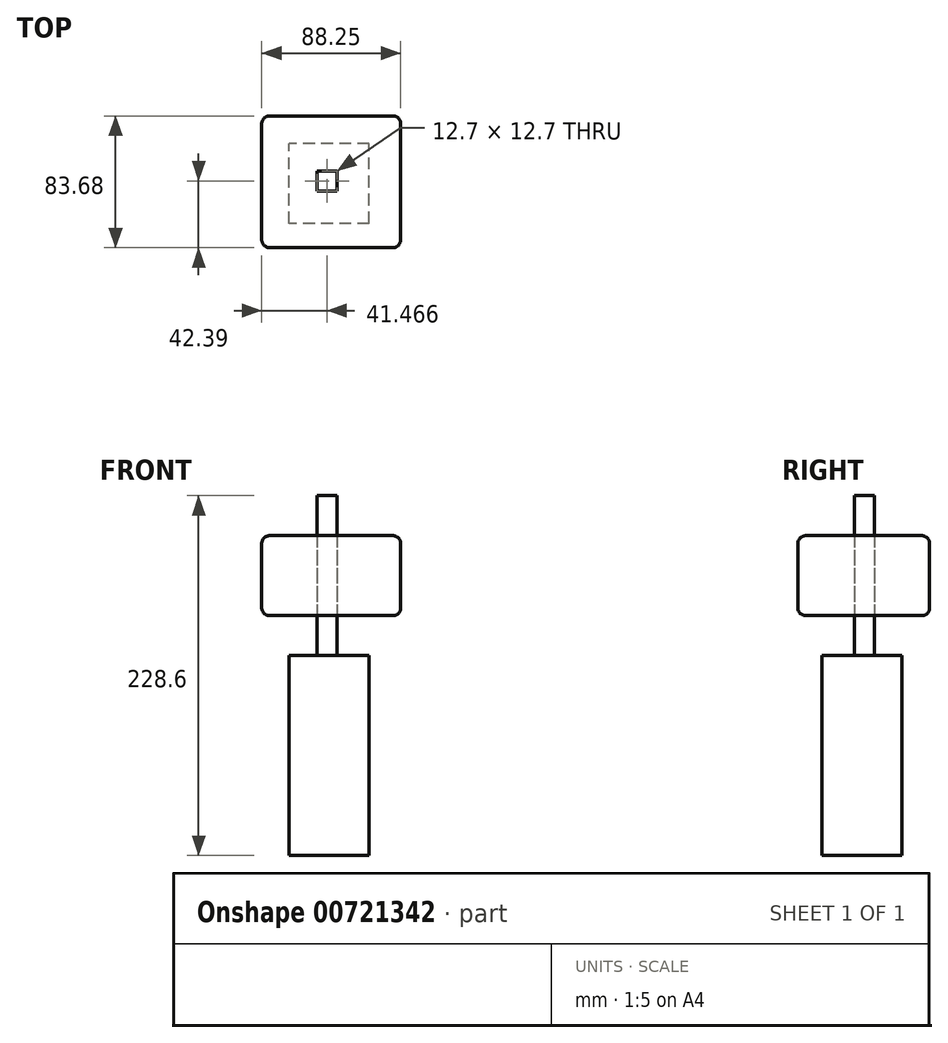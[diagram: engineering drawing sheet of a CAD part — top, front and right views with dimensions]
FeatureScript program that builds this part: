
annotation { "Feature Type Name" : "Feature", "Feature Type Description" : "" }
export const myFeature = defineFeature(function(context is Context, id is Id, definition is map)
    precondition{}
    {
        {
            var Q0;
            Q0=qCreatedBy(makeId("Front.planeOp"),FACE);
            var sketch = newSketch(context, id + "F0", { "sketchPlane" : qUnion([Q0])});
            skLineSegment(sketch, "E0.bottom", {"start": v(0, 0) * mm, "end": v(-50.8, 0) * mm});
            skLineSegment(sketch, "E0.top", {"start": v(0, 127) * mm, "end": v(-50.8, 127) * mm});
            skLineSegment(sketch, "E0.left", {"start": v(0, 0) * mm, "end": v(0, 127) * mm});
            skLineSegment(sketch, "E0.right", {"start": v(-50.8, 0) * mm, "end": v(-50.8, 127) * mm});
            skSolve(sketch);
        }
        {
            var Q0;
            Q0=makeQuery(id+"F0.imprint","IMPRINT",FACE,{"disambiguationData":[TD([[makeQuery(id+"F0.imprint","IMPRINT",EDGE,{"derivedFrom":sQuery(id+"F0.wireOp",EDGE,"E0.bottom")}),-1.0]])]});
            extrude(context, id + "F1", {"entities" : qUnion([Q0]), "depth" : 50.8 * mm, "offsetDistance" : 25.4 * mm});
        }
        {
            var Q0;
            Q0=makeQuery(id+"F1.opExtrude","SWEPT_FACE",FACE,{"disambiguationData":[OSD([sQuery(id+"F0.wireOp",EDGE,"E0.top")])]});
            var sketch = newSketch(context, id + "F2", { "sketchPlane" : qUnion([Q0])});
            skLineSegment(sketch, "E1.bottom", {"start": v(-20.43, -17.38) * mm, "end": v(-33.13, -17.38) * mm});
            skLineSegment(sketch, "E1.top", {"start": v(-20.43, -30.08) * mm, "end": v(-33.13, -30.08) * mm});
            skLineSegment(sketch, "E1.left", {"start": v(-20.43, -17.38) * mm, "end": v(-20.43, -30.08) * mm});
            skLineSegment(sketch, "E1.right", {"start": v(-33.13, -17.38) * mm, "end": v(-33.13, -30.08) * mm});
            skSolve(sketch);
        }
        {
            var Q0;
            Q0=makeQuery(id+"F2.imprint","IMPRINT",FACE,{"disambiguationData":[TD([[makeQuery(id+"F2.imprint","IMPRINT",EDGE,{"derivedFrom":sQuery(id+"F2.wireOp",EDGE,"E1.bottom")}),1.0]])]});
            extrude(context, id + "F3", {"entities" : qUnion([Q0]), "operationType" : NewBodyOperationType.ADD, "depth" : 25.4 * mm, "offsetDistance" : 25.4 * mm});
        }
        {
            var Q0;
            Q0=makeQuery(id+"F3.opExtrude","CAP_FACE",FACE,{"disambiguationData":[OSD([sQuery(id+"F2.wireOp",EDGE,"E1.bottom"),sQuery(id+"F2.wireOp",EDGE,"E1.top"),sQuery(id+"F2.wireOp",EDGE,"E1.left"),sQuery(id+"F2.wireOp",EDGE,"E1.right")])],"isStart":false});
            var sketch = newSketch(context, id + "F4", { "sketchPlane" : qUnion([Q0])});
            skLineSegment(sketch, "E2.bottom", {"start": v(20, 17.56) * mm, "end": v(-68.25, 17.56) * mm});
            skLineSegment(sketch, "E2.top", {"start": v(20, -66.12) * mm, "end": v(-68.25, -66.12) * mm});
            skLineSegment(sketch, "E2.left", {"start": v(20, 17.56) * mm, "end": v(20, -66.12) * mm});
            skLineSegment(sketch, "E2.right", {"start": v(-68.25, 17.56) * mm, "end": v(-68.25, -66.12) * mm});
            skSolve(sketch);
        }
        {
            var Q0;
            Q0=makeQuery(id+"F4.imprint","IMPRINT",FACE,{"disambiguationData":[TD([[makeQuery(id+"F4.imprint","IMPRINT",EDGE,{"derivedFrom":sQuery(id+"F4.wireOp",EDGE,"E2.bottom")}),1.0]])]});
            extrude(context, id + "F5", {"entities" : qUnion([Q0]), "depth" : 50.8 * mm, "offsetDistance" : 25.4 * mm});
        }
        {
            var Q0;
            Q0=makeQuery(id+"F3.opExtrude","CAP_FACE",FACE,{"disambiguationData":[OSD([sQuery(id+"F2.wireOp",EDGE,"E1.bottom"),sQuery(id+"F2.wireOp",EDGE,"E1.top"),sQuery(id+"F2.wireOp",EDGE,"E1.left"),sQuery(id+"F2.wireOp",EDGE,"E1.right")])],"isStart":false});
            extrude(context, id + "F6", {"entities" : qUnion([Q0]), "depth" : 76.2 * mm, "offsetDistance" : 25.4 * mm});
        }
        {
            var Q0;
            Q0=makeQuery(id+"F5.opExtrude","SWEPT_EDGE",EDGE,{"disambiguationData":[OSD([sQuery(id+"F4.wireOp",EDGE,"E2.bottom"),sQuery(id+"F4.wireOp",EDGE,"E2.left")])]});
            var Q1;
            Q1=makeQuery(id+"F5.opExtrude","CAP_EDGE",EDGE,{"disambiguationData":[OSD([sQuery(id+"F4.wireOp",EDGE,"E2.bottom")])],"isStart":false});
            var Q2;
            Q2=makeQuery(id+"F5.opExtrude","SWEPT_FACE",FACE,{"disambiguationData":[OSD([sQuery(id+"F4.wireOp",EDGE,"E2.bottom")])]});
            var Q3;
            Q3=makeQuery(id+"F5.opExtrude","SWEPT_EDGE",EDGE,{"disambiguationData":[OSD([sQuery(id+"F4.wireOp",EDGE,"E2.bottom"),sQuery(id+"F4.wireOp",EDGE,"E2.right")])]});
            var Q4;
            Q4=makeQuery(id+"F5.opExtrude","CAP_EDGE",EDGE,{"disambiguationData":[OSD([sQuery(id+"F4.wireOp",EDGE,"E2.right")])],"isStart":false});
            var Q5;
            Q5=makeQuery(id+"F5.opExtrude","CAP_EDGE",EDGE,{"disambiguationData":[OSD([sQuery(id+"F4.wireOp",EDGE,"E2.right")])],"isStart":true});
            var Q6;
            Q6=makeQuery(id+"F5.opExtrude","SWEPT_EDGE",EDGE,{"disambiguationData":[OSD([sQuery(id+"F4.wireOp",EDGE,"E2.top"),sQuery(id+"F4.wireOp",EDGE,"E2.right")])]});
            var Q7;
            Q7=makeQuery(id+"F5.opExtrude","CAP_EDGE",EDGE,{"disambiguationData":[OSD([sQuery(id+"F4.wireOp",EDGE,"E2.top")])],"isStart":false});
            var Q8;
            Q8=makeQuery(id+"F5.opExtrude","SWEPT_EDGE",EDGE,{"disambiguationData":[OSD([sQuery(id+"F4.wireOp",EDGE,"E2.top"),sQuery(id+"F4.wireOp",EDGE,"E2.left")])]});
            var Q9;
            Q9=makeQuery(id+"F5.opExtrude","CAP_EDGE",EDGE,{"disambiguationData":[OSD([sQuery(id+"F4.wireOp",EDGE,"E2.top")])],"isStart":true});
            var Q10;
            Q10=makeQuery(id+"F5.opExtrude","CAP_EDGE",EDGE,{"disambiguationData":[OSD([sQuery(id+"F4.wireOp",EDGE,"E2.left")])],"isStart":false});
            var Q11;
            Q11=makeQuery(id+"F5.opExtrude","CAP_EDGE",EDGE,{"disambiguationData":[OSD([sQuery(id+"F4.wireOp",EDGE,"E2.left")])],"isStart":true});
            fillet(context, id + "F7", {"entities" : qUnion([Q0, Q1, Q2, Q3, Q4, Q5, Q6, Q7, Q8, Q9, Q10, Q11]), "radius" : 5.08 * mm, "tangentPropagation" : true, "allowEdgeOverflow" : false});
        }
    });
